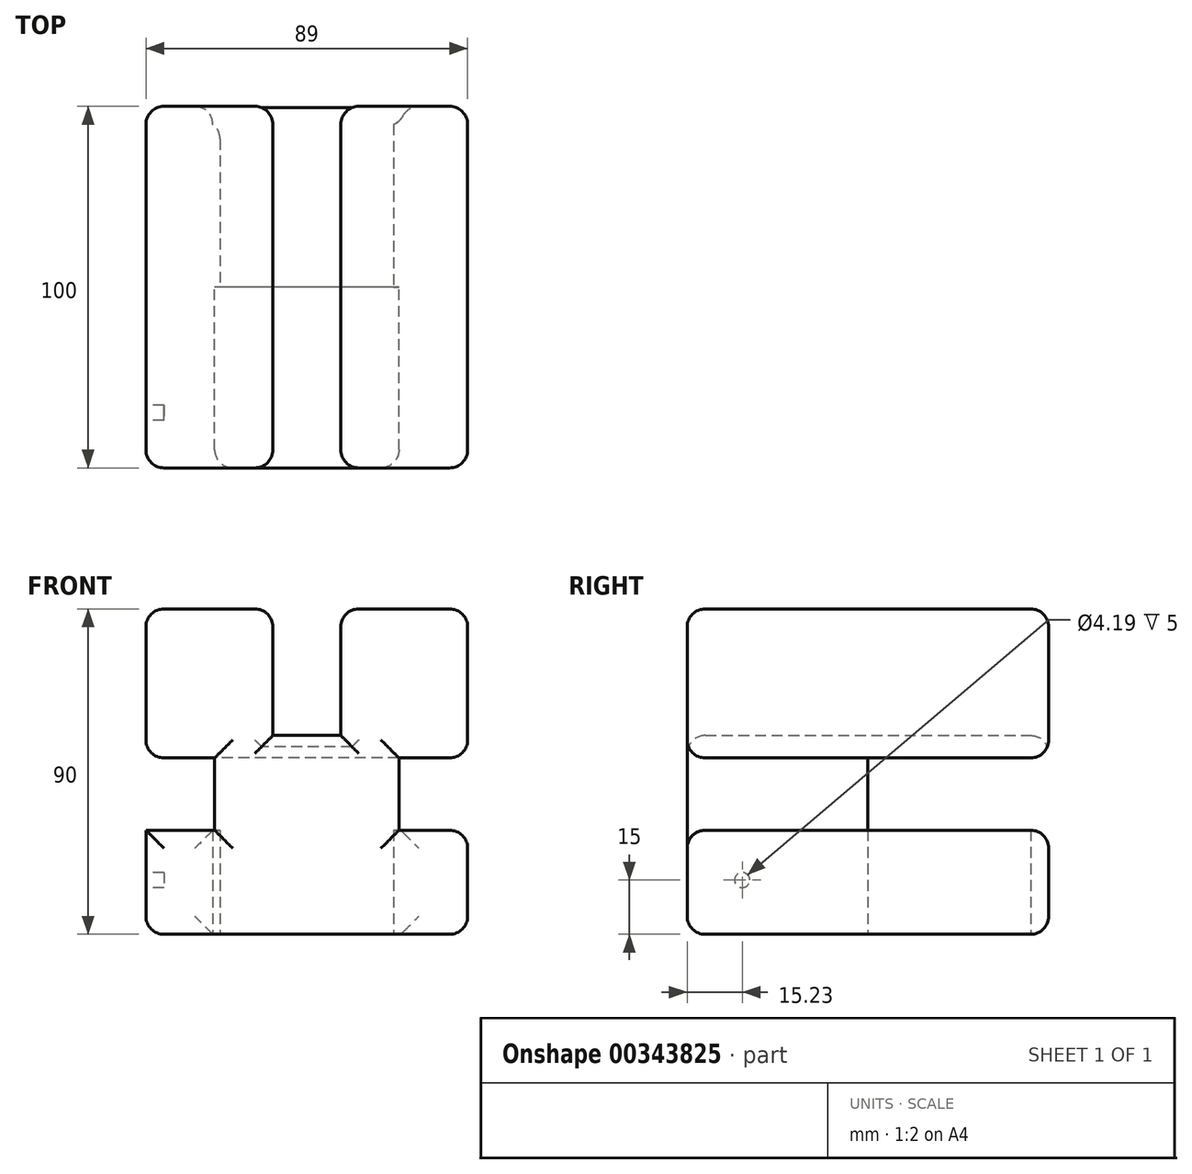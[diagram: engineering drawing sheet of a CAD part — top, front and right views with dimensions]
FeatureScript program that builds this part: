
annotation { "Feature Type Name" : "Feature", "Feature Type Description" : "" }
export const myFeature = defineFeature(function(context is Context, id is Id, definition is map)
    precondition{}
    {
        {
            var Q0;
            Q0=qCreatedBy(makeId("Front.planeOp"),FACE);
            var sketch = newSketch(context, id + "F0", { "sketchPlane" : qUnion([Q0])});
            skLineSegment(sketch, "E0.bottom", {"start": v(0, 0) * mm, "end": v(25.5, 0) * mm});
            skLineSegment(sketch, "E0.top", {"start": v(0, 75) * mm, "end": v(25.5, 75) * mm});
            skLineSegment(sketch, "E0.left", {"start": v(0, 0) * mm, "end": v(0, 75) * mm});
            skLineSegment(sketch, "E0.right", {"start": v(25.5, 0) * mm, "end": v(25.5, 75) * mm});
            skLineSegment(sketch, "E1.MirrorCS", {"start": v(-25.5, 0) * mm, "end": v(-25.5, 75) * mm});
            skLineSegment(sketch, "E2.MirrorCS", {"start": v(0, 0) * mm, "end": v(-25.5, 0) * mm});
            skLineSegment(sketch, "E3.MirrorCS", {"start": v(0, 75) * mm, "end": v(-25.5, 75) * mm});
            skLineSegment(sketch, "E4.bottom", {"start": v(-25.5, 26.28) * mm, "end": v(-44.5, 26.28) * mm});
            skLineSegment(sketch, "E4.top", {"start": v(-25.5, 33.78) * mm, "end": v(-44.5, 33.78) * mm});
            skLineSegment(sketch, "E4.left", {"start": v(-25.5, 26.28) * mm, "end": v(-25.5, 33.78) * mm});
            skLineSegment(sketch, "E4.right", {"start": v(-44.5, 26.28) * mm, "end": v(-44.5, 33.78) * mm});
            skLineSegment(sketch, "E5.MirrorCS", {"start": v(-25.5, 18.78) * mm, "end": v(-44.5, 18.78) * mm});
            skLineSegment(sketch, "E6.MirrorCS", {"start": v(-44.5, 26.28) * mm, "end": v(-44.5, 18.78) * mm});
            skLineSegment(sketch, "E7.bottom", {"start": v(-25.5, 75) * mm, "end": v(-44.5, 75) * mm});
            skLineSegment(sketch, "E7.top", {"start": v(-25.5, 0) * mm, "end": v(-44.5, 0) * mm});
            skLineSegment(sketch, "E7.left", {"start": v(-25.5, 75) * mm, "end": v(-25.5, 0) * mm});
            skLineSegment(sketch, "E7.right", {"start": v(-44.5, 75) * mm, "end": v(-44.5, 0) * mm});
            skLineSegment(sketch, "E8.MirrorCS", {"start": v(25.5, 33.78) * mm, "end": v(44.5, 33.78) * mm});
            skLineSegment(sketch, "E9.MirrorCS", {"start": v(25.5, 18.78) * mm, "end": v(44.5, 18.78) * mm});
            skLineSegment(sketch, "E10.MirrorCS", {"start": v(44.5, 75) * mm, "end": v(44.5, 0) * mm});
            skLineSegment(sketch, "E11.MirrorCS", {"start": v(25.5, 0) * mm, "end": v(44.5, 0) * mm});
            skLineSegment(sketch, "E12.MirrorCS", {"start": v(25.5, 75) * mm, "end": v(44.5, 75) * mm});
            skLineSegment(sketch, "E13.bottom", {"start": v(0, 75) * mm, "end": v(-9.4, 75) * mm});
            skLineSegment(sketch, "E13.top", {"start": v(0, 40) * mm, "end": v(-9.4, 40) * mm});
            skLineSegment(sketch, "E13.left", {"start": v(0, 75) * mm, "end": v(0, 40) * mm});
            skLineSegment(sketch, "E13.right", {"start": v(-9.4, 75) * mm, "end": v(-9.4, 40) * mm});
            skLineSegment(sketch, "E14.MirrorCS", {"start": v(9.4, 75) * mm, "end": v(9.4, 40) * mm});
            skLineSegment(sketch, "E15.MirrorCS", {"start": v(0, 40) * mm, "end": v(9.4, 40) * mm});
            skLineSegment(sketch, "E16", {"start": v(-25.5, 18.78) * mm, "end": v(-25.5, 0) * mm});
            skSolve(sketch);
        }
        {
            var Q0;
            {var subQ4=sQuery(id+"F0.wireOp",EDGE,"E2.MirrorCS");Q0=makeQuery(id+"F0.imprint","IMPRINT",FACE,{"disambiguationData":[TD([[makeQuery(id+"F0.imprint","IMPRINT",EDGE,{"derivedFrom":subQ4}),-1.0]])]});}
            var Q1;
            {var subQ0=sQuery(id+"F0.wireOp",EDGE,"E4.top");Q1=makeQuery(id+"F0.imprint","IMPRINT",FACE,{"disambiguationData":[TD([[makeQuery(id+"F0.imprint","IMPRINT",EDGE,{"derivedFrom":subQ0}),-1.0]])]});}
            var Q2;
            {var subQ2=sQuery(id+"F0.wireOp",EDGE,"E5.MirrorCS");Q2=makeQuery(id+"F0.imprint","IMPRINT",FACE,{"disambiguationData":[TD([[makeQuery(id+"F0.imprint","IMPRINT",EDGE,{"derivedFrom":subQ2}),1.0]])]});}
            var Q3;
            {var subQ1=sQuery(id+"F0.wireOp",EDGE,"E0.bottom");Q3=makeQuery(id+"F0.imprint","IMPRINT",FACE,{"disambiguationData":[TD([[makeQuery(id+"F0.imprint","IMPRINT",EDGE,{"derivedFrom":subQ1}),1.0]])]});}
            var Q4;
            {var subQ0=sQuery(id+"F0.wireOp",EDGE,"E8.MirrorCS");Q4=makeQuery(id+"F0.imprint","IMPRINT",FACE,{"disambiguationData":[TD([[makeQuery(id+"F0.imprint","IMPRINT",EDGE,{"derivedFrom":subQ0}),1.0]])]});}
            var Q5;
            {var subQ2=sQuery(id+"F0.wireOp",EDGE,"E9.MirrorCS");Q5=makeQuery(id+"F0.imprint","IMPRINT",FACE,{"disambiguationData":[TD([[makeQuery(id+"F0.imprint","IMPRINT",EDGE,{"derivedFrom":subQ2}),-1.0]])]});}
            extrude(context, id + "F1", {"entities" : qUnion([Q0, Q1, Q2, Q3, Q4, Q5]), "depth" : 100 * mm, "offsetDistance" : 25 * mm});
        }
        {
            var Q0;
            Q0=qCreatedBy(makeId("Top.planeOp"),FACE);
            var sketch = newSketch(context, id + "F2", { "sketchPlane" : qUnion([Q0])});
            skLineSegment(sketch, "E17.bottom", {"start": v(0, 0) * mm, "end": v(-26, 0) * mm});
            skLineSegment(sketch, "E17.top", {"start": v(0, -50) * mm, "end": v(-26, -50) * mm});
            skLineSegment(sketch, "E17.left", {"start": v(0, 0) * mm, "end": v(0, -50) * mm});
            skLineSegment(sketch, "E17.right", {"start": v(-26, 0) * mm, "end": v(-26, -50) * mm});
            skLineSegment(sketch, "E18.MirrorCS", {"start": v(0, -50) * mm, "end": v(26, -50) * mm});
            skLineSegment(sketch, "E19.MirrorCS", {"start": v(26, 0) * mm, "end": v(26, -50) * mm});
            skLineSegment(sketch, "E20.MirrorCS", {"start": v(0, 0) * mm, "end": v(26, 0) * mm});
            skSolve(sketch);
        }
        {
            var Q0;
            Q0=makeQuery(id+"F2.imprint","IMPRINT",FACE,{"disambiguationData":[TD([[makeQuery(id+"F2.imprint","IMPRINT",EDGE,{"derivedFrom":sQuery(id+"F2.wireOp",EDGE,"E17.bottom")}),1.0]])]});
            var Q1;
            Q1=makeQuery(id+"F2.imprint","IMPRINT",FACE,{"disambiguationData":[TD([[makeQuery(id+"F2.imprint","IMPRINT",EDGE,{"derivedFrom":sQuery(id+"F2.wireOp",EDGE,"E17.left")}),1.0]])]});
            extrude(context, id + "F3", {"entities" : qUnion([Q0, Q1]), "depth" : 33.78 * mm, "offsetDistance" : 25 * mm});
        }
        {
            var Q0;
            Q0=makeQuery(id+"F3.opExtrude","SWEPT_BODY",BODY,{"disambiguationData":[OSD([sQuery(id+"F2.wireOp",EDGE,"E17.bottom"),sQuery(id+"F2.wireOp",EDGE,"E17.top"),sQuery(id+"F2.wireOp",EDGE,"E17.right"),sQuery(id+"F2.wireOp",EDGE,"E18.MirrorCS"),sQuery(id+"F2.wireOp",EDGE,"E19.MirrorCS"),sQuery(id+"F2.wireOp",EDGE,"E20.MirrorCS")])]});
            var Q1;
            Q1=makeQuery(id+"F1.opExtrude","SWEPT_BODY",BODY,{"disambiguationData":[OSD([sQuery(id+"F0.wireOp",EDGE,"E0.bottom"),sQuery(id+"F0.wireOp",EDGE,"E0.top"),sQuery(id+"F0.wireOp",EDGE,"E0.right"),sQuery(id+"F0.wireOp",EDGE,"E1.MirrorCS"),sQuery(id+"F0.wireOp",EDGE,"E2.MirrorCS"),sQuery(id+"F0.wireOp",EDGE,"E3.MirrorCS"),sQuery(id+"F0.wireOp",EDGE,"E4.top"),sQuery(id+"F0.wireOp",EDGE,"E5.MirrorCS"),sQuery(id+"F0.wireOp",EDGE,"E7.bottom"),sQuery(id+"F0.wireOp",EDGE,"E7.top"),sQuery(id+"F0.wireOp",EDGE,"E7.right"),sQuery(id+"F0.wireOp",EDGE,"E8.MirrorCS"),sQuery(id+"F0.wireOp",EDGE,"E9.MirrorCS"),sQuery(id+"F0.wireOp",EDGE,"E10.MirrorCS"),sQuery(id+"F0.wireOp",EDGE,"E11.MirrorCS"),sQuery(id+"F0.wireOp",EDGE,"E12.MirrorCS"),sQuery(id+"F0.wireOp",EDGE,"E13.top"),sQuery(id+"F0.wireOp",EDGE,"E13.right"),sQuery(id+"F0.wireOp",EDGE,"E14.MirrorCS"),sQuery(id+"F0.wireOp",EDGE,"E15.MirrorCS")])]});
            booleanBodies(context, id + "F4", {"operationType" : BooleanOperationType.SUBTRACTION, "tools" : qUnion([Q0]), "targets" : qUnion([Q1])});
        }
        {
            var Q0;
            Q0=makeQuery(id+"F1.opExtrude","SWEPT_FACE",FACE,{"disambiguationData":[OSD([sQuery(id+"F0.wireOp",EDGE,"E0.bottom"),sQuery(id+"F0.wireOp",EDGE,"E2.MirrorCS"),sQuery(id+"F0.wireOp",EDGE,"E7.top"),sQuery(id+"F0.wireOp",EDGE,"E11.MirrorCS")])]});
            extrude(context, id + "F5", {"entities" : qUnion([Q0]), "operationType" : NewBodyOperationType.ADD, "depth" : 15 * mm, "offsetDistance" : 25 * mm});
        }
        {
            var Q0;
            Q0=makeQuery(id+"F1.opExtrude","SWEPT_FACE",FACE,{"disambiguationData":[OSD([sQuery(id+"F0.wireOp",EDGE,"E9.MirrorCS")])]});
            var Q1;
            Q1=makeQuery(id+"F1.opExtrude","SWEPT_FACE",FACE,{"disambiguationData":[OSD([sQuery(id+"F0.wireOp",EDGE,"E5.MirrorCS")])]});
            extrude(context, id + "F6", {"entities" : qUnion([Q0, Q1]), "operationType" : NewBodyOperationType.REMOVE, "oppositeDirection" : true, "depth" : 5 * mm, "offsetDistance" : 25 * mm});
        }
        {
            var Q0;
            Q0=makeQuery(id+"F1.opExtrude","SWEPT_FACE",FACE,{"disambiguationData":[OSD([sQuery(id+"F0.wireOp",EDGE,"E3.MirrorCS"),sQuery(id+"F0.wireOp",EDGE,"E7.bottom")])]});
            var Q1;
            Q1=makeQuery(id+"F1.opExtrude","SWEPT_FACE",FACE,{"disambiguationData":[OSD([sQuery(id+"F0.wireOp",EDGE,"E0.top"),sQuery(id+"F0.wireOp",EDGE,"E12.MirrorCS")])]});
            var Q2;
            {var subQ0=sQuery(id+"F0.wireOp",EDGE,"E11.MirrorCS");var subQ1=sQuery(id+"F0.wireOp",EDGE,"E7.top");var subQ2=sQuery(id+"F0.wireOp",EDGE,"E2.MirrorCS");var subQ3=sQuery(id+"F0.wireOp",EDGE,"E0.bottom");Q2=makeQuery(id+"F5.boolean.opBoolean","MERGE",FACE,{"derivedFrom":[makeQuery(id+"F1.opExtrude","CAP_FACE",FACE,{"disambiguationData":[OSD([subQ3,sQuery(id+"F0.wireOp",EDGE,"E0.top"),sQuery(id+"F0.wireOp",EDGE,"E0.right"),sQuery(id+"F0.wireOp",EDGE,"E1.MirrorCS"),subQ2,sQuery(id+"F0.wireOp",EDGE,"E3.MirrorCS"),sQuery(id+"F0.wireOp",EDGE,"E4.top"),sQuery(id+"F0.wireOp",EDGE,"E5.MirrorCS"),sQuery(id+"F0.wireOp",EDGE,"E7.bottom"),subQ1,sQuery(id+"F0.wireOp",EDGE,"E7.right"),sQuery(id+"F0.wireOp",EDGE,"E8.MirrorCS"),sQuery(id+"F0.wireOp",EDGE,"E9.MirrorCS"),sQuery(id+"F0.wireOp",EDGE,"E10.MirrorCS"),subQ0,sQuery(id+"F0.wireOp",EDGE,"E12.MirrorCS"),sQuery(id+"F0.wireOp",EDGE,"E13.top"),sQuery(id+"F0.wireOp",EDGE,"E13.right"),sQuery(id+"F0.wireOp",EDGE,"E14.MirrorCS"),sQuery(id+"F0.wireOp",EDGE,"E15.MirrorCS")])],"isStart":false}),makeQuery(id+"F5.opExtrude","SWEPT_FACE",FACE,{"disambiguationData":[OSD([subQ3,subQ2,subQ1,subQ0]),TDD([makeQuery(id+"F1.opExtrude","CAP_EDGE",EDGE,{"disambiguationData":[OSD([subQ3,subQ2,subQ1,subQ0])],"isStart":false})])]})]});}
            var Q3;
            {var subQ0=sQuery(id+"F0.wireOp",EDGE,"E7.right");var subQ1=sQuery(id+"F0.wireOp",EDGE,"E4.top");var subQ2=sQuery(id+"F0.wireOp",EDGE,"E7.bottom");var subQ3=sQuery(id+"F0.wireOp",EDGE,"E3.MirrorCS");var subQ4=sQuery(id+"F0.wireOp",EDGE,"E14.MirrorCS");var subQ5=sQuery(id+"F0.wireOp",EDGE,"E12.MirrorCS");var subQ6=sQuery(id+"F0.wireOp",EDGE,"E0.top");var subQ7=sQuery(id+"F0.wireOp",EDGE,"E8.MirrorCS");var subQ8=sQuery(id+"F0.wireOp",EDGE,"E10.MirrorCS");var subQ9=sQuery(id+"F0.wireOp",EDGE,"E15.MirrorCS");var subQ10=sQuery(id+"F0.wireOp",EDGE,"E13.top");var subQ11=sQuery(id+"F0.wireOp",EDGE,"E13.right");Q3=makeQuery(id+"F4.opBoolean","SPLIT",FACE,{"disambiguationData":[TD([makeQuery(id+"F1.opExtrude","SWEPT_FACE",FACE,{"disambiguationData":[OSD([subQ1])]})])],"derivedFrom":makeQuery(id+"F1.opExtrude","CAP_FACE",FACE,{"disambiguationData":[OSD([sQuery(id+"F0.wireOp",EDGE,"E0.bottom"),subQ6,sQuery(id+"F0.wireOp",EDGE,"E0.right"),sQuery(id+"F0.wireOp",EDGE,"E1.MirrorCS"),sQuery(id+"F0.wireOp",EDGE,"E2.MirrorCS"),subQ3,subQ1,sQuery(id+"F0.wireOp",EDGE,"E5.MirrorCS"),subQ2,sQuery(id+"F0.wireOp",EDGE,"E7.top"),subQ0,subQ7,sQuery(id+"F0.wireOp",EDGE,"E9.MirrorCS"),subQ8,sQuery(id+"F0.wireOp",EDGE,"E11.MirrorCS"),subQ5,subQ10,subQ11,subQ4,subQ9])],"isStart":true})});}
            var Q4;
            Q4=makeQuery(id+"F1.opExtrude","SWEPT_EDGE",EDGE,{"disambiguationData":[OSD([sQuery(id+"F0.wireOp",EDGE,"E4.top"),sQuery(id+"F0.wireOp",EDGE,"E4.right"),sQuery(id+"F0.wireOp",EDGE,"E7.right")])]});
            var Q5;
            {var subQ0=sQuery(id+"F0.wireOp",EDGE,"E11.MirrorCS");var subQ1=sQuery(id+"F0.wireOp",EDGE,"E10.MirrorCS");Q5=makeQuery(id+"F5.boolean.opBoolean","MERGE",FACE,{"derivedFrom":[makeQuery(id+"F1.opExtrude","SWEPT_FACE",FACE,{"disambiguationData":[OSD([subQ1]),TDD([makeQuery(id+"F0.imprint","IMPRINT",EDGE,{"disambiguationData":[TD([[makeQuery(id+"F0.imprint","INTERSECT",VERTEX,{"derivedFrom":[sQuery(id+"F0.wireOp",EDGE,"E9.MirrorCS"),subQ1]}),-1.0]])],"derivedFrom":subQ1})])]}),makeQuery(id+"F5.opExtrude","SWEPT_FACE",FACE,{"disambiguationData":[OSD([subQ1,subQ0])]})]});}
            var Q6;
            {var subQ0=sQuery(id+"F0.wireOp",EDGE,"E10.MirrorCS");Q6=makeQuery(id+"F1.opExtrude","SWEPT_FACE",FACE,{"disambiguationData":[OSD([subQ0]),TDD([makeQuery(id+"F0.imprint","IMPRINT",EDGE,{"disambiguationData":[TD([[makeQuery(id+"F0.imprint","INTERSECT",VERTEX,{"derivedFrom":[sQuery(id+"F0.wireOp",EDGE,"E8.MirrorCS"),subQ0]}),1.0]])],"derivedFrom":subQ0})])]});}
            var Q7;
            {var subQ0=sQuery(id+"F0.wireOp",EDGE,"E11.MirrorCS");var subQ1=sQuery(id+"F0.wireOp",EDGE,"E10.MirrorCS");var subQ2=sQuery(id+"F0.wireOp",EDGE,"E9.MirrorCS");var subQ3=sQuery(id+"F0.wireOp",EDGE,"E7.top");var subQ4=sQuery(id+"F0.wireOp",EDGE,"E2.MirrorCS");var subQ5=sQuery(id+"F0.wireOp",EDGE,"E0.bottom");var subQ6=makeQuery(id+"F1.opExtrude","CAP_FACE",FACE,{"disambiguationData":[OSD([subQ5,sQuery(id+"F0.wireOp",EDGE,"E0.top"),sQuery(id+"F0.wireOp",EDGE,"E0.right"),sQuery(id+"F0.wireOp",EDGE,"E1.MirrorCS"),subQ4,sQuery(id+"F0.wireOp",EDGE,"E3.MirrorCS"),sQuery(id+"F0.wireOp",EDGE,"E4.top"),sQuery(id+"F0.wireOp",EDGE,"E5.MirrorCS"),sQuery(id+"F0.wireOp",EDGE,"E7.bottom"),subQ3,sQuery(id+"F0.wireOp",EDGE,"E7.right"),sQuery(id+"F0.wireOp",EDGE,"E8.MirrorCS"),subQ2,subQ1,subQ0,sQuery(id+"F0.wireOp",EDGE,"E12.MirrorCS"),sQuery(id+"F0.wireOp",EDGE,"E13.top"),sQuery(id+"F0.wireOp",EDGE,"E13.right"),sQuery(id+"F0.wireOp",EDGE,"E14.MirrorCS"),sQuery(id+"F0.wireOp",EDGE,"E15.MirrorCS")])],"isStart":true});var subQ9=makeQuery(id+"F3.opExtrude","SWEPT_FACE",FACE,{"disambiguationData":[OSD([sQuery(id+"F2.wireOp",EDGE,"E19.MirrorCS")])]});Q7=makeQuery(id+"F5.boolean.opBoolean","MERGE",FACE,{"derivedFrom":[makeQuery(id+"F4.opBoolean","SPLIT",FACE,{"disambiguationData":[TD([makeQuery(id+"F1.opExtrude","SWEPT_FACE",FACE,{"disambiguationData":[OSD([subQ2])]})])],"derivedFrom":subQ6}),makeQuery(id+"F5.opExtrude","SWEPT_FACE",FACE,{"disambiguationData":[OSD([subQ5,subQ4,subQ3,subQ0]),TDD([makeQuery(id+"F4.opBoolean","SPLIT",EDGE,{"disambiguationData":[TD([subQ9])],"derivedFrom":makeQuery(id+"F1.opExtrude","CAP_EDGE",EDGE,{"disambiguationData":[OSD([subQ5,subQ4,subQ3,subQ0])],"isStart":true})})])]})]});}
            var Q8;
            {var subQ0=sQuery(id+"F0.wireOp",EDGE,"E11.MirrorCS");var subQ1=sQuery(id+"F0.wireOp",EDGE,"E7.right");var subQ2=sQuery(id+"F0.wireOp",EDGE,"E7.top");var subQ3=sQuery(id+"F0.wireOp",EDGE,"E5.MirrorCS");var subQ4=sQuery(id+"F0.wireOp",EDGE,"E2.MirrorCS");var subQ5=sQuery(id+"F0.wireOp",EDGE,"E0.bottom");var subQ6=makeQuery(id+"F1.opExtrude","CAP_FACE",FACE,{"disambiguationData":[OSD([subQ5,sQuery(id+"F0.wireOp",EDGE,"E0.top"),sQuery(id+"F0.wireOp",EDGE,"E0.right"),sQuery(id+"F0.wireOp",EDGE,"E1.MirrorCS"),subQ4,sQuery(id+"F0.wireOp",EDGE,"E3.MirrorCS"),sQuery(id+"F0.wireOp",EDGE,"E4.top"),subQ3,sQuery(id+"F0.wireOp",EDGE,"E7.bottom"),subQ2,subQ1,sQuery(id+"F0.wireOp",EDGE,"E8.MirrorCS"),sQuery(id+"F0.wireOp",EDGE,"E9.MirrorCS"),sQuery(id+"F0.wireOp",EDGE,"E10.MirrorCS"),subQ0,sQuery(id+"F0.wireOp",EDGE,"E12.MirrorCS"),sQuery(id+"F0.wireOp",EDGE,"E13.top"),sQuery(id+"F0.wireOp",EDGE,"E13.right"),sQuery(id+"F0.wireOp",EDGE,"E14.MirrorCS"),sQuery(id+"F0.wireOp",EDGE,"E15.MirrorCS")])],"isStart":true});var subQ9=makeQuery(id+"F3.opExtrude","SWEPT_FACE",FACE,{"disambiguationData":[OSD([sQuery(id+"F2.wireOp",EDGE,"E17.right")])]});Q8=makeQuery(id+"F5.boolean.opBoolean","MERGE",FACE,{"derivedFrom":[makeQuery(id+"F4.opBoolean","SPLIT",FACE,{"disambiguationData":[TD([makeQuery(id+"F1.opExtrude","SWEPT_FACE",FACE,{"disambiguationData":[OSD([subQ3])]})])],"derivedFrom":subQ6}),makeQuery(id+"F5.opExtrude","SWEPT_FACE",FACE,{"disambiguationData":[OSD([subQ5,subQ4,subQ2,subQ0]),TDD([makeQuery(id+"F4.opBoolean","SPLIT",EDGE,{"disambiguationData":[TD([subQ9])],"derivedFrom":makeQuery(id+"F1.opExtrude","CAP_EDGE",EDGE,{"disambiguationData":[OSD([subQ5,subQ4,subQ2,subQ0])],"isStart":true})})])]})]});}
            var Q9;
            Q9=makeQuery(id+"F6.boolean.opBoolean","COPY",EDGE,{"derivedFrom":makeQuery(id+"F6.opExtrude","CAP_EDGE",EDGE,{"disambiguationData":[OSD([sQuery(id+"F0.wireOp",EDGE,"E5.MirrorCS"),sQuery(id+"F0.wireOp",EDGE,"E6.MirrorCS"),sQuery(id+"F0.wireOp",EDGE,"E7.right")])],"isStart":false})});
            var Q10;
            Q10=makeQuery(id+"F5.opExtrude","CAP_EDGE",EDGE,{"disambiguationData":[OSD([sQuery(id+"F0.wireOp",EDGE,"E7.top"),sQuery(id+"F0.wireOp",EDGE,"E7.right")])],"isStart":false});
            fillet(context, id + "F7", {"entities" : qUnion([Q0, Q1, Q2, Q3, Q4, Q5, Q6, Q7, Q8, Q9, Q10]), "radius" : 5 * mm, "tangentPropagation" : true, "allowEdgeOverflow" : false});
        }
        {
            var Q0;
            {var subQ0=sQuery(id+"F2.wireOp",EDGE,"E17.right");Q0=makeQuery(id+"F5.boolean.opBoolean","MERGE",FACE,{"derivedFrom":[makeQuery(id+"F4.opBoolean","COPY",FACE,{"derivedFrom":makeQuery(id+"F3.opExtrude","SWEPT_FACE",FACE,{"disambiguationData":[OSD([subQ0])]})}),makeQuery(id+"F5.opExtrude","SWEPT_FACE",FACE,{"disambiguationData":[OSD([subQ0])]})]});}
            extrude(context, id + "F8", {"entities" : qUnion([Q0]), "operationType" : NewBodyOperationType.ADD, "depth" : 2 * mm, "offsetDistance" : 25 * mm});
        }
        {
            var Q0;
            {var subQ0=sQuery(id+"F2.wireOp",EDGE,"E19.MirrorCS");Q0=makeQuery(id+"F5.boolean.opBoolean","MERGE",FACE,{"derivedFrom":[makeQuery(id+"F4.opBoolean","COPY",FACE,{"derivedFrom":makeQuery(id+"F3.opExtrude","SWEPT_FACE",FACE,{"disambiguationData":[OSD([subQ0])]})}),makeQuery(id+"F5.opExtrude","SWEPT_FACE",FACE,{"disambiguationData":[OSD([subQ0])]})]});}
            extrude(context, id + "F9", {"entities" : qUnion([Q0]), "operationType" : NewBodyOperationType.ADD, "depth" : 2 * mm, "offsetDistance" : 25 * mm});
        }
        {
            var Q0;
            Q0=makeQuery(id+"F8.opExtrude","CAP_EDGE",EDGE,{"disambiguationData":[OSD([sQuery(id+"F2.wireOp",EDGE,"E17.bottom"),sQuery(id+"F2.wireOp",EDGE,"E17.right")])],"isStart":false});
            var Q1;
            {var subQ0=sQuery(id+"F2.wireOp",EDGE,"E20.MirrorCS");var subQ1=sQuery(id+"F2.wireOp",EDGE,"E19.MirrorCS");Q1=makeQuery(id+"F9.boolean.opBoolean","MERGE",EDGE,{"derivedFrom":[makeQuery(id+"F7.opFillet","BLEND_EDGE",EDGE,{"blendedFrom":[makeQuery(id+"F5.boolean.opBoolean","MERGE",EDGE,{"derivedFrom":[makeQuery(id+"F4.opBoolean","COPY",EDGE,{"derivedFrom":makeQuery(id+"F3.opExtrude","SWEPT_EDGE",EDGE,{"disambiguationData":[OSD([subQ1,subQ0])]})}),makeQuery(id+"F5.opExtrude","SWEPT_EDGE",EDGE,{"disambiguationData":[OSD([subQ1,subQ0])]})]}),makeQuery(id+"F5.boolean.opBoolean","MERGE",FACE,{"derivedFrom":[makeQuery(id+"F4.opBoolean","COPY",FACE,{"derivedFrom":makeQuery(id+"F3.opExtrude","SWEPT_FACE",FACE,{"disambiguationData":[OSD([subQ1])]})}),makeQuery(id+"F5.opExtrude","SWEPT_FACE",FACE,{"disambiguationData":[OSD([subQ1])]})]})],"blendedInto":[makeQuery(id+"F5.boolean.opBoolean","MERGE",FACE,{"derivedFrom":[makeQuery(id+"F4.opBoolean","COPY",FACE,{"derivedFrom":makeQuery(id+"F3.opExtrude","SWEPT_FACE",FACE,{"disambiguationData":[OSD([subQ1])]})}),makeQuery(id+"F5.opExtrude","SWEPT_FACE",FACE,{"disambiguationData":[OSD([subQ1])]})]})]}),makeQuery(id+"F9.opExtrude","CAP_EDGE",EDGE,{"disambiguationData":[OSD([subQ1,subQ0])],"isStart":true})]});}
            fillet(context, id + "F10", {"entities" : qUnion([Q0, Q1]), "radius" : 5 * mm, "tangentPropagation" : true, "allowEdgeOverflow" : false});
        }
        {
            var Q0;
            {var subQ0=sQuery(id+"F0.wireOp",EDGE,"E7.right");var subQ1=sQuery(id+"F0.wireOp",EDGE,"E7.top");Q0=makeQuery(id+"F5.boolean.opBoolean","MERGE",FACE,{"derivedFrom":[makeQuery(id+"F1.opExtrude","SWEPT_FACE",FACE,{"disambiguationData":[OSD([subQ0]),TDD([makeQuery(id+"F0.imprint","IMPRINT",EDGE,{"disambiguationData":[TD([[makeQuery(id+"F0.imprint","INTERSECT",VERTEX,{"derivedFrom":[subQ1,subQ0]}),1.0]])],"derivedFrom":subQ0})])]}),makeQuery(id+"F5.opExtrude","SWEPT_FACE",FACE,{"disambiguationData":[OSD([subQ1,subQ0])]})]});}
            var sketch = newSketch(context, id + "F11", { "sketchPlane" : qUnion([Q0])});
            skCircle(sketch, "E21", {"center": v(84.77, 0) * mm, "radius": 2.1 * mm});
            skSolve(sketch);
        }
        {
            var Q0;
            Q0 = qSketchRegion(id + "F11", true);
            extrude(context, id + "F12", {"entities" : qUnion([Q0]), "operationType" : NewBodyOperationType.REMOVE, "oppositeDirection" : true, "depth" : 5 * mm, "offsetDistance" : 25 * mm});
        }
    });
